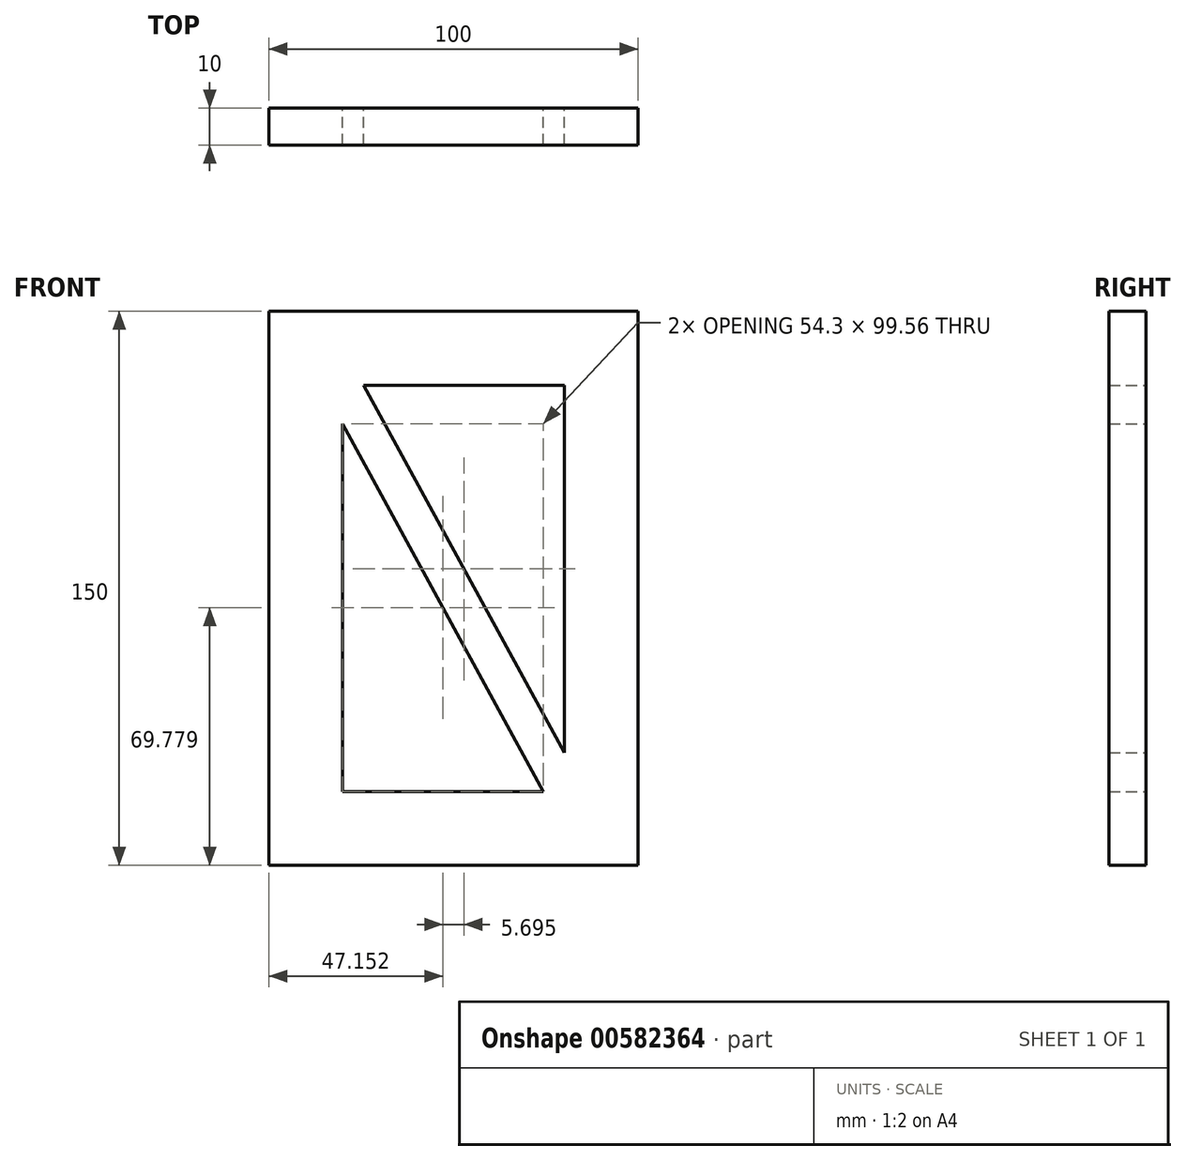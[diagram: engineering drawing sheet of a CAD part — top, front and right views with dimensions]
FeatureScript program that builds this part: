
annotation { "Feature Type Name" : "Feature", "Feature Type Description" : "" }
export const myFeature = defineFeature(function(context is Context, id is Id, definition is map)
    precondition{}
    {
        {
            var Q0;
            Q0=qCreatedBy(makeId("Front.planeOp"),FACE);
            var sketch = newSketch(context, id + "F0", { "sketchPlane" : qUnion([Q0])});
            skLineSegment(sketch, "E0.bottom", {"start": v(50, 75) * mm, "end": v(-50, 75) * mm});
            skLineSegment(sketch, "E0.top", {"start": v(50, -75) * mm, "end": v(-50, -75) * mm});
            skLineSegment(sketch, "E0.left", {"start": v(50, 75) * mm, "end": v(50, -75) * mm});
            skLineSegment(sketch, "E0.right", {"start": v(-50, 75) * mm, "end": v(-50, -75) * mm});
            skPoint(sketch, "E0.middle", {"position": v(0, 0) * mm});
            skLineSegment(sketch, "E1.0", {"start": v(30, 55) * mm, "end": v(30, -44.56) * mm});
            skLineSegment(sketch, "E1.1", {"start": v(30, 55) * mm, "end": v(-24.3, 55) * mm});
            skLineSegment(sketch, "E1.2", {"start": v(-30, 44.56) * mm, "end": v(-30, -55) * mm});
            skLineSegment(sketch, "E1.3", {"start": v(24.3, -55) * mm, "end": v(-30, -55) * mm});
            skLineSegment(sketch, "E2", {"start": v(-30, 55) * mm, "end": v(30, -55) * mm, "construction": true});
            skLineSegment(sketch, "E3.0", {"start": v(-30, 44.56) * mm, "end": v(24.3, -55) * mm});
            skLineSegment(sketch, "E4.0", {"start": v(-24.3, 55) * mm, "end": v(30, -44.56) * mm});
            skSolve(sketch);
        }
        {
            var Q0;
            Q0=makeQuery(id+"F0.imprint","IMPRINT",FACE,{"disambiguationData":[TD([[makeQuery(id+"F0.imprint","IMPRINT",EDGE,{"derivedFrom":sQuery(id+"F0.wireOp",EDGE,"E0.bottom")}),1.0]])]});
            extrude(context, id + "F1", {"entities" : qUnion([Q0]), "depth" : 10 * mm, "offsetDistance" : 25 * mm});
        }
    });
